# Revit family: Kohler ForeFront 2661IN-0 Family
name_source: partatom
category: Plumbing Fixtures
revit_build: Autodesk Revit 2018 (Build: 20180329_1100(x64)
units: mm (PartAtom-declared; Revit-internal decimal feet)

## family parameters
Cut with Voids When Loaded = No
Host = Face
OmniClass Number = 23.45.05.14.14
OmniClass Title = Sinks/Lavatories
Part Type = Normal
Room Calculation Point = No
Round Connector Dimension = Use Diameter
Shared = No

## types (1)
- Kohler 2661IN-0
    CW Connection = No
    CWFU = 0
    Default Elevation = 864 mm
    Description = Vessel square without mixer hole in white
    Drain Diameter = 44 mm
    Finish = Vitreous China - Kohler - 0 - White
    HW Connection = No
    HWFU = 0
    Height = 175 mm
    Length = 413 mm
    Manufacturer = Kohler
    Model = Kohler ForeFront 2661
    Sanitary Connector = Sanitary Drain
    Type Image = 2661IN-0.tif
    URL = http://www.us.kohler.com
    Vent Connection = No
    WFU = 0
    Waste Connection = Yes
    Width = 413 mm
    length1 = 575 mm

## geometry (parser evidence)
native form markers: Sweep x2
no freeform markers — native parametric forms only
